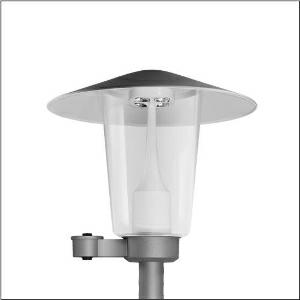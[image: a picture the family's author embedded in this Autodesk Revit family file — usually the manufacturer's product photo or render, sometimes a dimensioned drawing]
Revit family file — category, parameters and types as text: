
# Revit family: pilzleuchte_iq___st1_2a_5xa5235ev14h000022_0315
name_source: partatom
category: Lighting Fixtures
units: mm (PartAtom-declared; Revit-internal decimal feet)

## family parameters
Cut with Voids When Loaded = No
Host = Face
Light Source = No
Part Type = Normal
Room Calculation Point = No
Round Connector Dimension = Use Diameter
Shared = No

## types (1)
- --- (1 x LED, 1550 lm, 10.7 W, 3000K)
    Apparent Load = 11 VA
    CIE Flux Codes = 24 61 93 98 100
    Color Rendering = 70
    Color Temperature = 3000K
    Default Elevation = 1800 mm
    Description = Mushroom Luminaire iQ, mast luminaire, Module 540 iQ-SR, primary light control with 3 zone facetted reflector, of plastic, silver coated, highly specular, structured, primary optical cover: cover, of PMMA, transparent, light distribution: ST1.2a, light emission: direct distribution, primary light characteristic: asymmetric, installation type: post-top, LED, High Power LED, rated luminous flux: 1.550lm, luminous efficacy: 145lm/W, light colour: 730, colour temperature: 3000K, control gear: iQ-Street Remote, D4i with power reduction, control: optimised constant luminous flux control (CLO 2.0), Desk-Remote (wireless, voltage-free reading and setting of iQ features in the workshop via application-optimized NFC function/RFID function), Light-Fading, Smart-Wire, Night-Set, Lumen-Switch, Temp-Guard, Auto-Match, Street-Remote, pre-setting: logarithmic dimming characteristic, with terminal, 6-pole, max. 2.5mm², mains connection: 230..240V, AC, 50/60Hz, connection cable pre-assembled, cable length: 5,5m, wiring characteristics: H07RN-F, start of lifetime: 11W, end of service life: 11W, reduction: 6W, luminaire housing, upper part, of glass-fibre reinforced polyester, coated, Siteco® metallic grey (DB 702S), diameter: 650mm, height: 586mm, spigot size: d x l = 76 x 70mm (post-top) | with reducer (optional accessory) 60 x 70mm, mounting height: 3..5m, post-top mast mounting element, of diecast aluminium, coated, Siteco® metallic grey (DB 702S), Module 540 iQ-SR, traffic white (RAL 9016), equipment: standard, Smart Interface above, protection rating (complete): IP65, insulation class (complete): insulation class II (safety insulation), certification: CE, ENEC, VDE, packaging unit: 1 piece

Light Distribution: ST1.2a
    Height = 586 mm
    Lamp = 1 x LED
    Lamp Light Flux = 1550 lm
    Lamp Power = 10.7 W
    Lamp count = 1
    Length = 650 mm
    Luminous efficacy = 145 lm/W
    Manufacturer = Siteco
    ModVariant = No
    Model = 5XA5235EV14H000022
    Number of Poles = 1
    OnlyDefault = Yes
    Power Factor = 1
    Product Name = Pilzleuchte iQ | ST1.2a
    Product group = mast luminaire | pylon top
    ProductGroupID = 6100
    Protection Class = Protection class II
    Protection Degree = IP 65
    RLX_Detail_Level = 1
    RLX_Emergency_Light_Flux = 0 lm
    RLX_Emergency_Type = 0
    RLX_Emergency_Type_DB = No
    RlxData = <blob elided: 51705 chars, md5=d8961927>
    Socket = socket
    Standby Power = 0 W
    System Light Flux = 1550 lm
    System Power = 11 W
    Type Comments = factory setting: luminous flux: 100 % | dim-lin: 254 | 419 mA
    Type Image = l_1006957.jpg
    URL = http://relux.com
    VarID = @adj_086820
    Voltage = 0 V
    Weight = 0.00 kg
    Width = 0 mm  [stored 0 ft]

note: [stored X ft] marks values corroborated as IEEE doubles in the binary element streams (Revit-internal decimal feet)

## geometry (parser evidence)
native form markers: Blend x4, Sweep x13
no freeform markers — native parametric forms only
